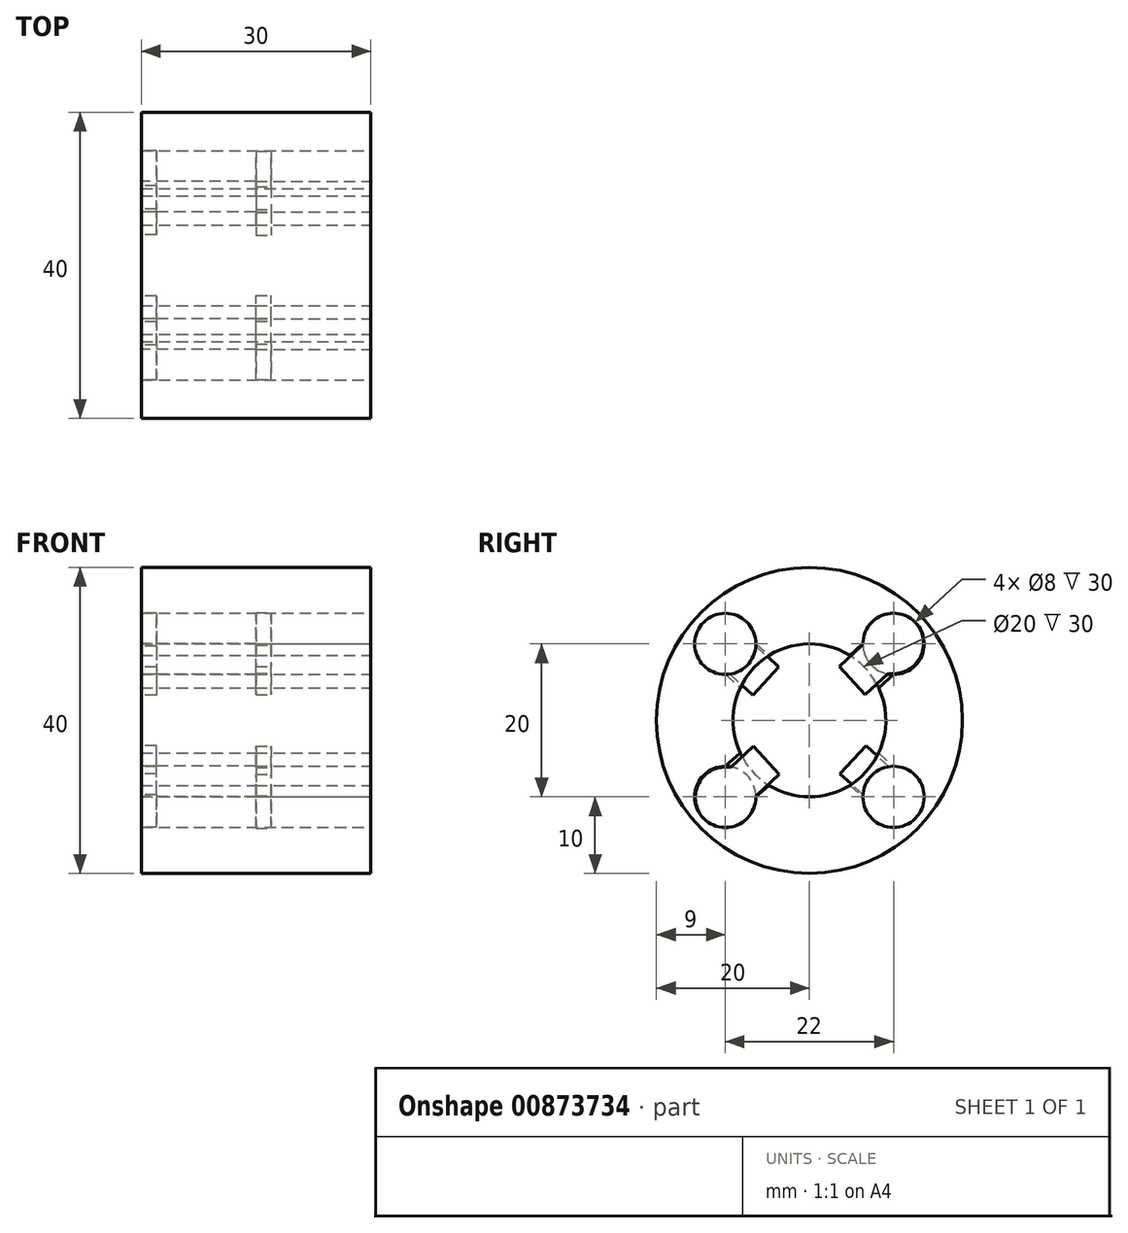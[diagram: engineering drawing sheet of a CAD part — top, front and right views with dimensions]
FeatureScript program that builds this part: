
annotation { "Feature Type Name" : "Feature", "Feature Type Description" : "" }
export const myFeature = defineFeature(function(context is Context, id is Id, definition is map)
    precondition{}
    {
        {
            var Q0;
            Q0=qCreatedBy(makeId("Right.planeOp"),FACE);
            var sketch = newSketch(context, id + "F0", { "sketchPlane" : qUnion([Q0])});
            skCircle(sketch, "E0", {"center": v(0, 0) * mm, "radius": 20 * mm});
            skCircle(sketch, "E1", {"center": v(0, 0) * mm, "radius": 10 * mm});
            skSolve(sketch);
        }
        {
            var Q0;
            Q0 = qSketchRegion(id + "F0", true);
            extrude(context, id + "F1", {"entities" : qUnion([Q0]), "oppositeDirection" : true, "depth" : 30 * mm, "offsetDistance" : 25 * mm});
        }
        {
            var Q0;
            Q0=qCreatedBy(makeId("Right.planeOp"),FACE);
            var sketch = newSketch(context, id + "F2", { "sketchPlane" : qUnion([Q0])});
            skCircle(sketch, "E2", {"center": v(-11, 10) * mm, "radius": 4 * mm});
            skCircle(sketch, "E3.MirrorC", {"center": v(11, 10) * mm, "radius": 4 * mm});
            skCircle(sketch, "E4.MirrorC", {"center": v(-11, -10) * mm, "radius": 4 * mm});
            skCircle(sketch, "E5.MirrorC", {"center": v(11, -10) * mm, "radius": 4 * mm});
            skSolve(sketch);
        }
        {
            var Q0;
            Q0 = qSketchRegion(id + "F2", true);
            extrude(context, id + "F3", {"entities" : qUnion([Q0]), "operationType" : NewBodyOperationType.REMOVE, "oppositeDirection" : true, "depth" : 30 * mm, "offsetDistance" : 25 * mm});
        }
        {
            var Q0;
            Q0=qCreatedBy(makeId("Right.planeOp"),FACE);
            var sketch = newSketch(context, id + "F4", { "sketchPlane" : qUnion([Q0])});
            skLineSegment(sketch, "E6.bottom", {"start": v(-11, -10) * mm, "end": v(-7, -10) * mm});
            skLineSegment(sketch, "E6.top", {"start": v(7, 10) * mm, "end": v(11, 10) * mm});
            skLineSegment(sketch, "E6.left", {"start": v(-11, -10) * mm, "end": v(-11, -6) * mm});
            skLineSegment(sketch, "E6.right", {"start": v(11, 6) * mm, "end": v(11, 10) * mm});
            skPoint(sketch, "E6.middle", {"position": v(0, 0) * mm});
            skCircle(sketch, "E7", {"center": v(11, 10) * mm, "radius": 4 * mm});
            skCircle(sketch, "E8", {"center": v(-11, -10) * mm, "radius": 4 * mm});
            skLineSegment(sketch, "E9", {"start": v(-11, -6) * mm, "end": v(7, 10) * mm});
            skLineSegment(sketch, "E10", {"start": v(-7, -10) * mm, "end": v(11, 6) * mm});
            skPoint(sketch, "E11.orphan", {"position": v(-11, 10) * mm});
            skPoint(sketch, "E12.orphan", {"position": v(11, -10) * mm});
            skSolve(sketch);
        }
        {
            var Q0;
            Q0 = qSketchRegion(id + "F4", true);
            extrude(context, id + "F5", {"entities" : qUnion([Q0]), "operationType" : NewBodyOperationType.REMOVE, "oppositeDirection" : true, "depth" : 15 * mm, "offsetDistance" : 25 * mm});
        }
        {
            var Q0;
            Q0=qCreatedBy(makeId("Right.planeOp"),FACE);
            cPlane(context, id + "F6", {"entities" : qUnion([Q0]), "cplaneType" : CPlaneType.OFFSET, "offset" : 30 * mm, "oppositeDirection" : true, "width" : 150 * mm, "height" : 150 * mm});
        }
        {
            var Q0;
            Q0=qCreatedBy(id+"F6.planeOp",FACE);
            var sketch = newSketch(context, id + "F7", { "sketchPlane" : qUnion([Q0])});
            skLineSegment(sketch, "E13.bottom", {"start": v(-7, 10) * mm, "end": v(-11, 10) * mm});
            skLineSegment(sketch, "E13.top", {"start": v(11, -10) * mm, "end": v(7, -10) * mm});
            skLineSegment(sketch, "E13.left", {"start": v(11, -6) * mm, "end": v(11, -10) * mm});
            skLineSegment(sketch, "E13.right", {"start": v(-11, 10) * mm, "end": v(-11, 6) * mm});
            skPoint(sketch, "E13.middle", {"position": v(0, 0) * mm});
            skCircle(sketch, "E14", {"center": v(-11, 10) * mm, "radius": 4 * mm});
            skCircle(sketch, "E15", {"center": v(11, -10) * mm, "radius": 4 * mm});
            skLineSegment(sketch, "E16", {"start": v(-11, 6) * mm, "end": v(7, -10) * mm});
            skLineSegment(sketch, "E17", {"start": v(-7, 10) * mm, "end": v(11, -6) * mm});
            skPoint(sketch, "E18.orphan", {"position": v(-11, -10) * mm});
            skPoint(sketch, "E19.orphan", {"position": v(11, 10) * mm});
            skSolve(sketch);
        }
        {
            var Q0;
            Q0 = qSketchRegion(id + "F7", true);
            extrude(context, id + "F8", {"entities" : qUnion([Q0]), "operationType" : NewBodyOperationType.REMOVE, "depth" : 15 * mm, "offsetDistance" : 25 * mm});
        }
        {
            var Q0;
            Q0=qCreatedBy(id+"F6.planeOp",FACE);
            var sketch = newSketch(context, id + "F9", { "sketchPlane" : qUnion([Q0])});
            skCircle(sketch, "E20", {"center": v(11, -10) * mm, "radius": 4 * mm});
            skLineSegment(sketch, "E21", {"start": v(11, -10) * mm, "end": v(5.7, -5.14) * mm});
            skLineSegment(sketch, "E22.0", {"start": v(13.28, -8.7) * mm, "end": v(7.38, -3.3) * mm});
            skLineSegment(sketch, "E23.0", {"start": v(9.9, -12.39) * mm, "end": v(4, -6.98) * mm});
            skLineSegment(sketch, "E24", {"start": v(13.28, -8.7) * mm, "end": v(9.9, -12.39) * mm});
            skLineSegment(sketch, "E25", {"start": v(4, -6.98) * mm, "end": v(7.38, -3.3) * mm});
            skSolve(sketch);
        }
        {
            var Q0;
            Q0 = qSketchRegion(id + "F9", true);
            extrude(context, id + "F10", {"entities" : qUnion([Q0]), "depth" : 2 * mm, "offsetDistance" : 25 * mm});
        }
        {
            var Q0;
            Q0=makeQuery(id+"F10.opExtrude","SWEPT_BODY",BODY,{"disambiguationData":[OSD([sQuery(id+"F9.wireOp",EDGE,"E20"),sQuery(id+"F9.wireOp",EDGE,"E22.0"),sQuery(id+"F9.wireOp",EDGE,"E23.0"),sQuery(id+"F9.wireOp",EDGE,"E25")])]});
            var Q1;
            Q1=makeQuery(id+"F1.opExtrude","CAP_EDGE",EDGE,{"disambiguationData":[OSD([sQuery(id+"F0.wireOp",EDGE,"E0")])],"isStart":false});
            circularPattern(context, id + "F11", {"entities" : qUnion([Q0]), "axis" : qUnion([Q1]), "angle" : 360 * degree, "instanceCount" : 4, "equalSpace" : true});
        }
        {
            var Q0;
            Q0=qCreatedBy(makeId("Right.planeOp"),FACE);
            cPlane(context, id + "F12", {"entities" : qUnion([Q0]), "cplaneType" : CPlaneType.OFFSET, "offset" : 15 * mm, "oppositeDirection" : true, "width" : 150 * mm, "height" : 150 * mm});
        }
        {
            var Q0;
            Q0=makeQuery(id+"F11.opPattern","COPY",BODY,{"derivedFrom":makeQuery(id+"F10.opExtrude","SWEPT_BODY",BODY,{"disambiguationData":[OSD([sQuery(id+"F9.wireOp",EDGE,"E20"),sQuery(id+"F9.wireOp",EDGE,"E22.0"),sQuery(id+"F9.wireOp",EDGE,"E23.0"),sQuery(id+"F9.wireOp",EDGE,"E25")])]}),"instanceName":"1"});
            var Q1;
            Q1=makeQuery(id+"F11.opPattern","COPY",BODY,{"derivedFrom":makeQuery(id+"F10.opExtrude","SWEPT_BODY",BODY,{"disambiguationData":[OSD([sQuery(id+"F9.wireOp",EDGE,"E20"),sQuery(id+"F9.wireOp",EDGE,"E22.0"),sQuery(id+"F9.wireOp",EDGE,"E23.0"),sQuery(id+"F9.wireOp",EDGE,"E25")])]}),"instanceName":"3"});
            var Q2;
            Q2=qCreatedBy(id+"F12.planeOp",FACE);
            mirror(context, id + "F13", {"entities" : qUnion([Q0, Q1]), "mirrorPlane" : qUnion([Q2])});
        }
        {
            var Q0;
            Q0=makeQuery(id+"F11.opPattern","COPY",BODY,{"derivedFrom":makeQuery(id+"F10.opExtrude","SWEPT_BODY",BODY,{"disambiguationData":[OSD([sQuery(id+"F9.wireOp",EDGE,"E20"),sQuery(id+"F9.wireOp",EDGE,"E22.0"),sQuery(id+"F9.wireOp",EDGE,"E23.0"),sQuery(id+"F9.wireOp",EDGE,"E25")])]}),"instanceName":"1"});
            var Q1;
            Q1=makeQuery(id+"F11.opPattern","COPY",BODY,{"derivedFrom":makeQuery(id+"F10.opExtrude","SWEPT_BODY",BODY,{"disambiguationData":[OSD([sQuery(id+"F9.wireOp",EDGE,"E20"),sQuery(id+"F9.wireOp",EDGE,"E22.0"),sQuery(id+"F9.wireOp",EDGE,"E23.0"),sQuery(id+"F9.wireOp",EDGE,"E25")])]}),"instanceName":"3"});
            deleteBodies(context, id + "F14", {"entities" : qUnion([Q0, Q1])});
        }
        {
            var Q0;
            Q0=makeQuery(id+"F13.opPattern","COPY",BODY,{"derivedFrom":makeQuery(id+"F11.opPattern","COPY",BODY,{"derivedFrom":makeQuery(id+"F10.opExtrude","SWEPT_BODY",BODY,{"disambiguationData":[OSD([sQuery(id+"F9.wireOp",EDGE,"E20"),sQuery(id+"F9.wireOp",EDGE,"E22.0"),sQuery(id+"F9.wireOp",EDGE,"E23.0"),sQuery(id+"F9.wireOp",EDGE,"E25")])]}),"instanceName":"1"}),"instanceName":"1"});
            var Q1;
            Q1=makeQuery(id+"F13.opPattern","COPY",BODY,{"derivedFrom":makeQuery(id+"F11.opPattern","COPY",BODY,{"derivedFrom":makeQuery(id+"F10.opExtrude","SWEPT_BODY",BODY,{"disambiguationData":[OSD([sQuery(id+"F9.wireOp",EDGE,"E20"),sQuery(id+"F9.wireOp",EDGE,"E22.0"),sQuery(id+"F9.wireOp",EDGE,"E23.0"),sQuery(id+"F9.wireOp",EDGE,"E25")])]}),"instanceName":"3"}),"instanceName":"1"});
            var Q2;
            Q2=makeQuery(id+"F1.opExtrude","SWEPT_FACE",FACE,{"disambiguationData":[OSD([sQuery(id+"F0.wireOp",EDGE,"E1")])]});
            transform(context, id + "F15", {"entities" : qUnion([Q0, Q1]), "transformType" : TransformType.ROTATION, "transformAxis" : qUnion([Q2]), "angle" : 5 * degree, "makeCopy" : false});
        }
        {
            var Q0;
            Q0=qCreatedBy(makeId("Front.planeOp"),FACE);
            var sketch = newSketch(context, id + "F16", { "sketchPlane" : qUnion([Q0])});
            skLineSegment(sketch, "E26", {"start": v(75.33, 0) * mm, "end": v(-76.26, 0) * mm});
            skSolve(sketch);
        }
        {
            var Q0;
            Q0=makeQuery(id+"F13.opPattern","COPY",BODY,{"derivedFrom":makeQuery(id+"F11.opPattern","COPY",BODY,{"derivedFrom":makeQuery(id+"F10.opExtrude","SWEPT_BODY",BODY,{"disambiguationData":[OSD([sQuery(id+"F9.wireOp",EDGE,"E20"),sQuery(id+"F9.wireOp",EDGE,"E22.0"),sQuery(id+"F9.wireOp",EDGE,"E23.0"),sQuery(id+"F9.wireOp",EDGE,"E25")])]}),"instanceName":"3"}),"instanceName":"1"});
            var Q1;
            Q1=makeQuery(id+"F13.opPattern","COPY",BODY,{"derivedFrom":makeQuery(id+"F11.opPattern","COPY",BODY,{"derivedFrom":makeQuery(id+"F10.opExtrude","SWEPT_BODY",BODY,{"disambiguationData":[OSD([sQuery(id+"F9.wireOp",EDGE,"E20"),sQuery(id+"F9.wireOp",EDGE,"E22.0"),sQuery(id+"F9.wireOp",EDGE,"E23.0"),sQuery(id+"F9.wireOp",EDGE,"E25")])]}),"instanceName":"1"}),"instanceName":"1"});
            var Q2;
            Q2=sQuery(id+"F16.wireOp",EDGE,"E26");
            var Q3;
            Q3=sQuery(id+"F16.wireOp",EDGE,"E26");
            transform(context, id + "F17", {"entities" : qUnion([Q0, Q1]), "transformType" : TransformType.TRANSLATION_DISTANCE, "transformDirection" : qUnion([Q3]), "distance" : 13 * mm, "makeCopy" : false});
        }
    });
